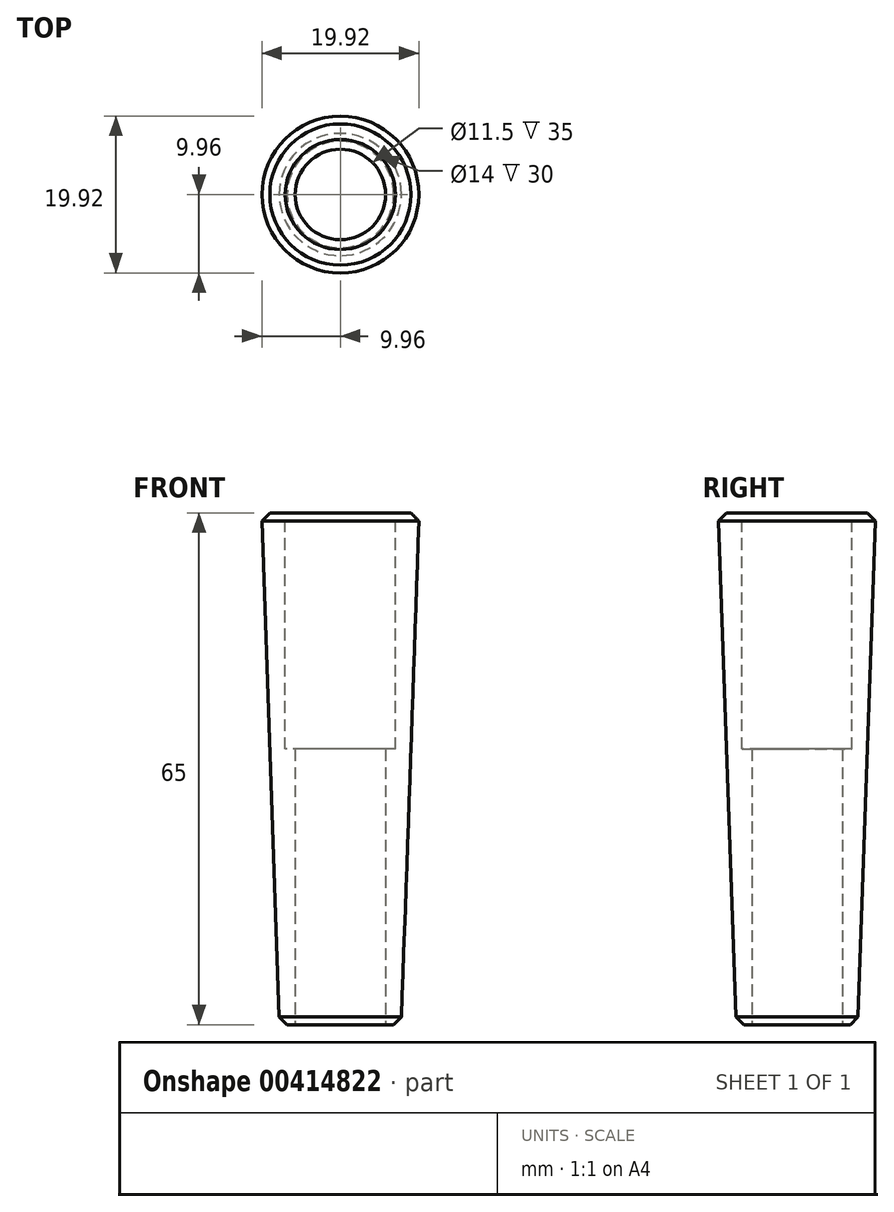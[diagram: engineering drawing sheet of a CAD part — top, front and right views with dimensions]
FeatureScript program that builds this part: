
annotation { "Feature Type Name" : "Feature", "Feature Type Description" : "" }
export const myFeature = defineFeature(function(context is Context, id is Id, definition is map)
    precondition{}
    {
        {
            var Q0;
            Q0=qCreatedBy(makeId("Top.planeOp"),FACE);
            var sketch = newSketch(context, id + "F0", { "sketchPlane" : qUnion([Q0])});
            skCircle(sketch, "E0", {"center": v(0, 0) * mm, "radius": 10 * mm});
            skCircle(sketch, "E1", {"center": v(0, 0) * mm, "radius": 7.5 * mm});
            skSolve(sketch);
        }
        {
            var Q0;
            Q0=makeQuery(id+"F0.imprint","IMPRINT",FACE,{"disambiguationData":[TD([[makeQuery(id+"F0.imprint","IMPRINT",EDGE,{"derivedFrom":sQuery(id+"F0.wireOp",EDGE,"E0")}),1.0]])]});
            var Q1;
            Q1=makeQuery(id+"F0.imprint","IMPRINT",FACE,{"disambiguationData":[TD([[makeQuery(id+"F0.imprint","IMPRINT",EDGE,{"derivedFrom":sQuery(id+"F0.wireOp",EDGE,"E1")}),1.0]])]});
            extrude(context, id + "F1", {"entities" : qUnion([Q0, Q1]), "depth" : 65 * mm});
        }
        {
            var Q0;
            Q0=qCreatedBy(makeId("Top.planeOp"),FACE);
            var sketch = newSketch(context, id + "F2", { "sketchPlane" : qUnion([Q0])});
            skCircle(sketch, "E2", {"center": v(0, 0) * mm, "radius": 5.75 * mm});
            skSolve(sketch);
        }
        {
            var Q0;
            Q0=makeQuery(id+"F2.imprint","IMPRINT",FACE,{"disambiguationData":[TD([[makeQuery(id+"F2.imprint","IMPRINT",EDGE,{"derivedFrom":sQuery(id+"F2.wireOp",EDGE,"E2")}),1.0]])]});
            extrude(context, id + "F3", {"entities" : qUnion([Q0]), "operationType" : NewBodyOperationType.REMOVE, "depth" : 35 * mm});
        }
        {
            var Q0;
            Q0=makeQuery(id+"F1.opExtrude","CAP_FACE",FACE,{"disambiguationData":[OSD([sQuery(id+"F0.wireOp",EDGE,"E0")])],"isStart":false});
            var sketch = newSketch(context, id + "F4", { "sketchPlane" : qUnion([Q0])});
            skCircle(sketch, "E3", {"center": v(0, 0) * mm, "radius": 7 * mm});
            skSolve(sketch);
        }
        {
            var Q0;
            Q0=makeQuery(id+"F4.imprint","IMPRINT",FACE,{"disambiguationData":[TD([[makeQuery(id+"F4.imprint","IMPRINT",EDGE,{"derivedFrom":sQuery(id+"F4.wireOp",EDGE,"E3")}),1.0]])]});
            extrude(context, id + "F5", {"entities" : qUnion([Q0]), "operationType" : NewBodyOperationType.REMOVE, "oppositeDirection" : true, "depth" : 30 * mm});
        }
        {
            var Q0;
            Q0=makeQuery(id+"F1.opExtrude","CAP_EDGE",EDGE,{"disambiguationData":[OSD([sQuery(id+"F0.wireOp",EDGE,"E0")])],"isStart":true});
            chamfer(context, id + "F6", {"entities" : qUnion([Q0]), "chamferType" : ChamferType.OFFSET_ANGLE, "width" : 65 * mm, "oppositeDirection" : false, "angle" : 2 * degree, "tangentPropagation" : true});
        }
        {
            var Q0;
            {var subQ0=sQuery(id+"F0.wireOp",EDGE,"E0");Q0=makeQuery(id+"F6.opChamfer","BLEND_EDGE",EDGE,{"blendedFrom":[makeQuery(id+"F1.opExtrude","CAP_EDGE",EDGE,{"disambiguationData":[OSD([subQ0])],"isStart":true}),makeQuery(id+"F1.opExtrude","CAP_FACE",FACE,{"disambiguationData":[OSD([subQ0])],"isStart":false})],"blendedInto":[makeQuery(id+"F1.opExtrude","CAP_FACE",FACE,{"disambiguationData":[OSD([subQ0])],"isStart":false})]});}
            var Q1;
            {var subQ0=sQuery(id+"F0.wireOp",EDGE,"E0");Q1=makeQuery(id+"F6.opChamfer","BLEND_EDGE",EDGE,{"blendedFrom":[makeQuery(id+"F1.opExtrude","CAP_EDGE",EDGE,{"disambiguationData":[OSD([subQ0])],"isStart":true}),makeQuery(id+"F1.opExtrude","CAP_FACE",FACE,{"disambiguationData":[OSD([subQ0])],"isStart":true})],"blendedInto":[makeQuery(id+"F1.opExtrude","CAP_FACE",FACE,{"disambiguationData":[OSD([subQ0])],"isStart":true})]});}
            chamfer(context, id + "F7", {"entities" : qUnion([Q0, Q1]), "width" : 1 * mm, "tangentPropagation" : true});
        }
    });
